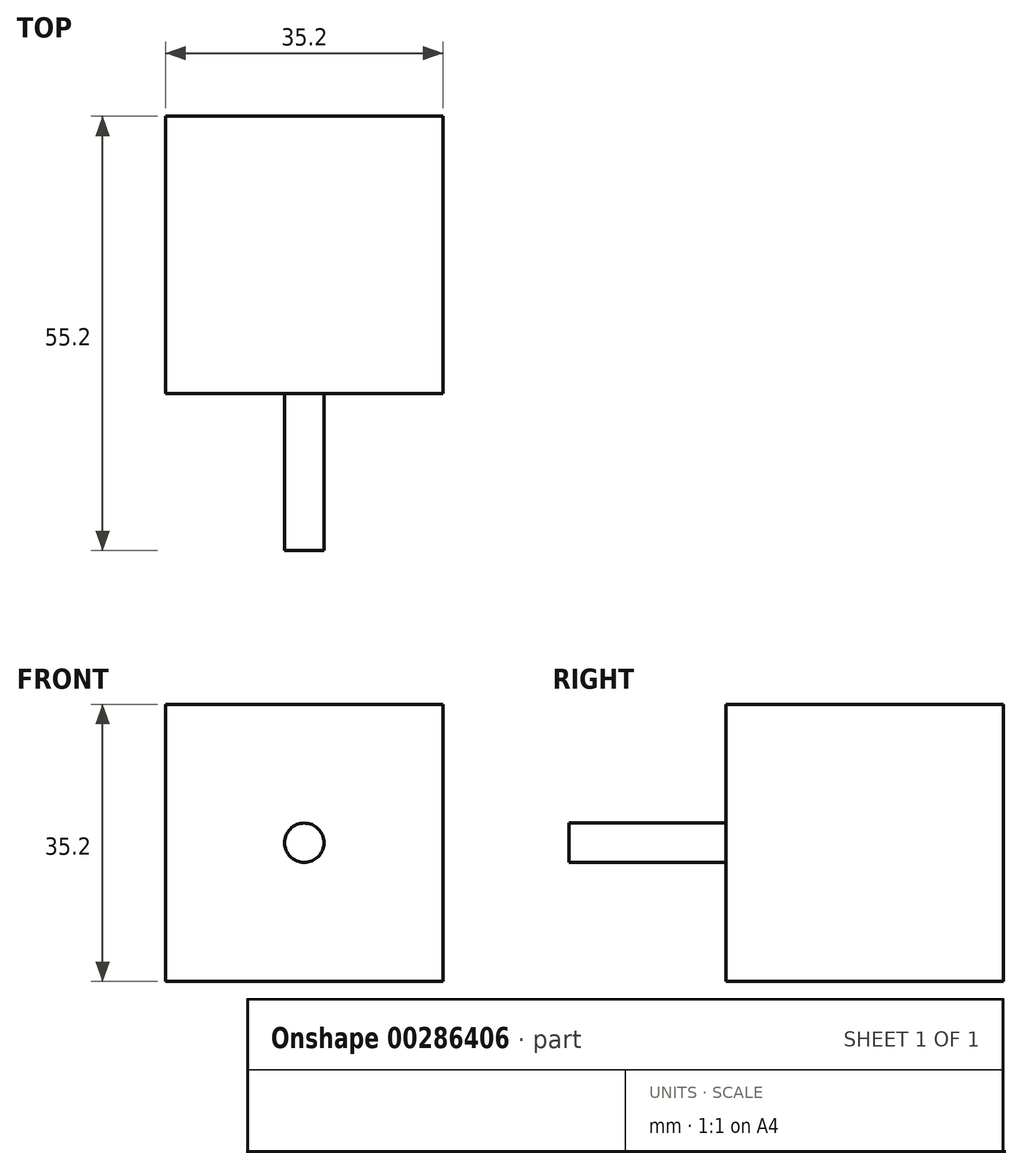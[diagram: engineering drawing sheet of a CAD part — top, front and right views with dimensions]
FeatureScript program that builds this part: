
annotation { "Feature Type Name" : "Feature", "Feature Type Description" : "" }
export const myFeature = defineFeature(function(context is Context, id is Id, definition is map)
    precondition{}
    {
        {
            var Q0;
            Q0=qCreatedBy(makeId("Front.planeOp"),FACE);
            var sketch = newSketch(context, id + "F0", { "sketchPlane" : qUnion([Q0])});
            skLineSegment(sketch, "E0.bottom", {"start": v(-17.6, 17.6) * mm, "end": v(17.6, 17.6) * mm});
            skLineSegment(sketch, "E0.top", {"start": v(-17.6, -17.6) * mm, "end": v(17.6, -17.6) * mm});
            skLineSegment(sketch, "E0.left", {"start": v(-17.6, 17.6) * mm, "end": v(-17.6, -17.6) * mm});
            skLineSegment(sketch, "E0.right", {"start": v(17.6, 17.6) * mm, "end": v(17.6, -17.6) * mm});
            skPoint(sketch, "E0.middle", {"position": v(0, 0) * mm});
            skSolve(sketch);
        }
        {
            var Q0;
            Q0=makeQuery(id+"F0.imprint","IMPRINT",FACE,{"disambiguationData":[TD([[makeQuery(id+"F0.imprint","IMPRINT",EDGE,{"derivedFrom":sQuery(id+"F0.wireOp",EDGE,"E0.bottom")}),-1.0]])]});
            extrude(context, id + "F1", {"entities" : qUnion([Q0]), "depth" : 35.2 * mm});
        }
        {
            var Q0;
            Q0=makeQuery(id+"F1.opExtrude","CAP_FACE",FACE,{"disambiguationData":[OSD([sQuery(id+"F0.wireOp",EDGE,"E0.bottom"),sQuery(id+"F0.wireOp",EDGE,"E0.top"),sQuery(id+"F0.wireOp",EDGE,"E0.left"),sQuery(id+"F0.wireOp",EDGE,"E0.right")])],"isStart":false});
            var sketch = newSketch(context, id + "F2", { "sketchPlane" : qUnion([Q0])});
            skCircle(sketch, "E1", {"center": v(0, 0) * mm, "radius": 2.5 * mm});
            skSolve(sketch);
        }
        {
            var Q0;
            Q0 = qSketchRegion(id + "F2", true);
            extrude(context, id + "F3", {"entities" : qUnion([Q0]), "operationType" : NewBodyOperationType.ADD, "depth" : 20 * mm});
        }
    });
